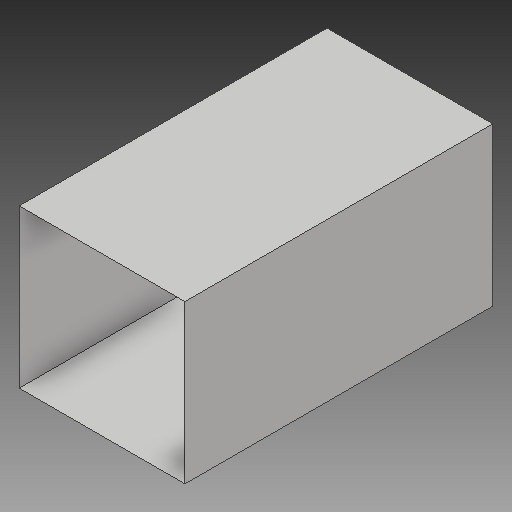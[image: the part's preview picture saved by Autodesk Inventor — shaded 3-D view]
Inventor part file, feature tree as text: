
AUTODESK INVENTOR PART (.ipt)
format: ipt  version: 2017 (Build 210142000, 142)  size: 89,600 bytes
history: native  units: in
note: dims shown in document units (in); Inventor stores cm internally (conversion verified against a paired STEP export)
features: other x2, sketch x1
ambient origin geometry x8: Origin, YZ Plane, XZ Plane, XY Plane, X Axis, Y Axis, Z Axis, Center Point
bodies: Solid1 (feature_tree)
feature tree (3):
  other  "corridor"
  other  "removed ends"
  sketch  "Sketch1"  dims[d0=6.6667in d1=7.0in d2=13.0in d3=0.0in]
